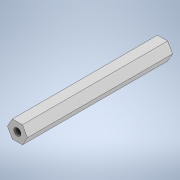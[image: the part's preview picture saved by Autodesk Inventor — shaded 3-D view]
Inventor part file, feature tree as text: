
AUTODESK INVENTOR PART (.ipt)
format: ipt  version: 2020 (Build 240168000, 168)  size: 110,080 bytes
history: native  units: in
note: dims shown in document units (in); Inventor stores cm internally (conversion verified against a paired STEP export)
features: sketch x2, extrude x1, hole x1, plane x1, mirror x1, projected_geometry x1
ambient origin geometry x8: Origin, YZ Plane, XZ Plane, XY Plane, X Axis, Y Axis, Z Axis, Center Point
bodies: Solid1 (feature_tree)
feature tree (7):
  extrude  "Extrusion1"  Depth=1.9685in TaperAngle=0.0deg
  hole  "Hole1"  [1 undecoded]
  plane  "Work Plane1"
  mirror  "Mirror1"
  sketch  "Sketch1"  dims[d0=0.2362in d1=1.9685in d2=0.0in]
  sketch  "Sketch2"  dims[d3=0.0968in d4=0.2953in d5=0.1575in d6=0.0787in d7=90.0deg d8=0.2953in d9=0.0in]
  projected_geometry  "Projected Loop1"
note: 1 required parameter value undecoded (feature->parameter linkage not recoverable at this tier; creation-order binding heuristic only, values carry confidence <= 0.55)
